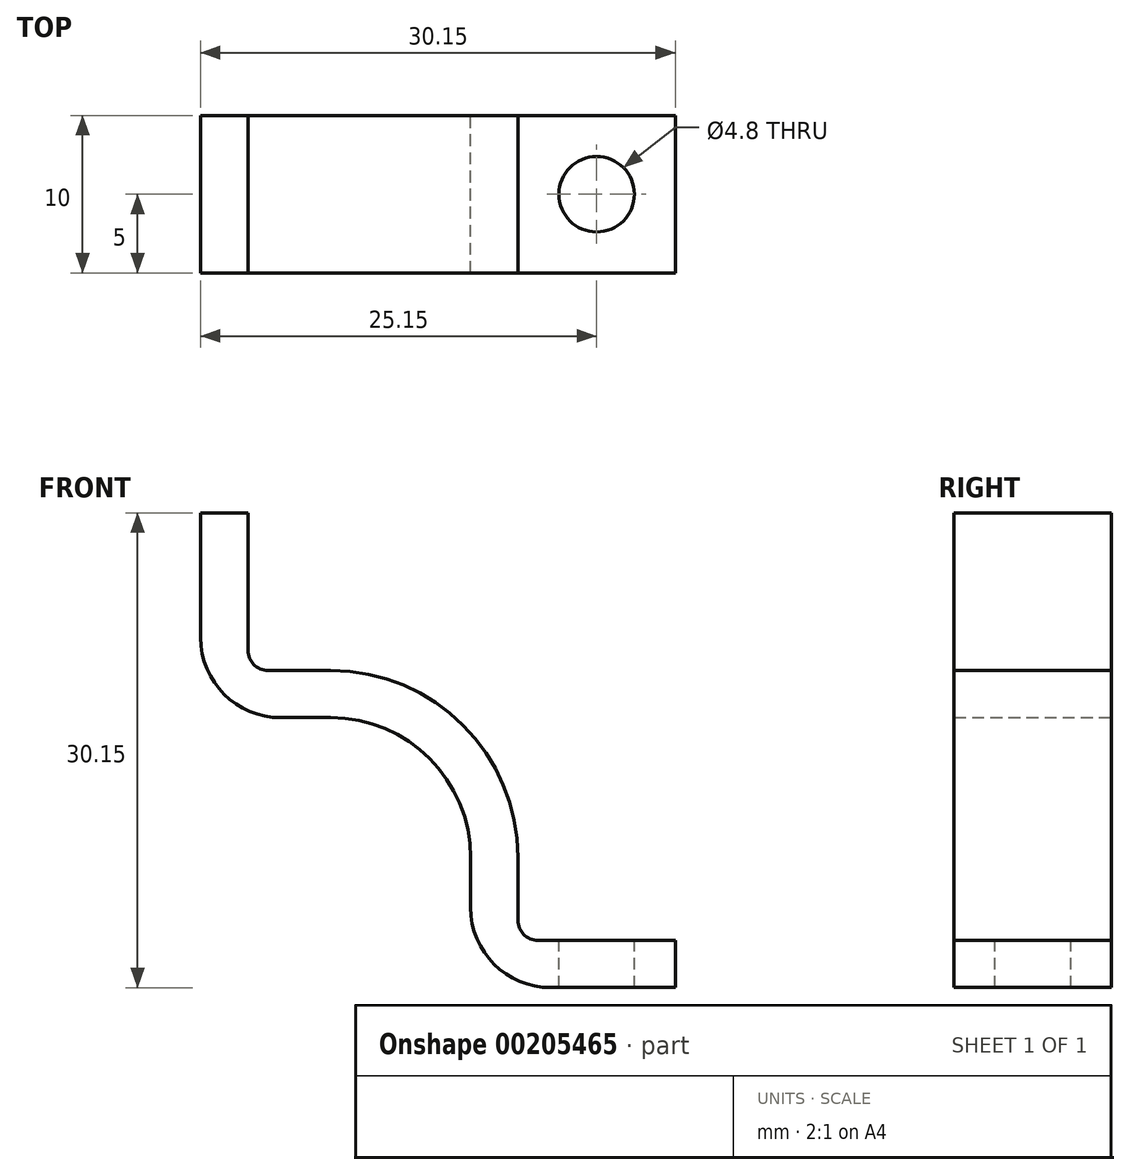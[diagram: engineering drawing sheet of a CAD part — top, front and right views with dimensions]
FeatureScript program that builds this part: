
annotation { "Feature Type Name" : "Feature", "Feature Type Description" : "" }
export const myFeature = defineFeature(function(context is Context, id is Id, definition is map)
    precondition{}
    {
        {
            var Q0;
            Q0=qCreatedBy(makeId("Front.planeOp"),FACE);
            var sketch = newSketch(context, id + "F0", { "sketchPlane" : qUnion([Q0])});
            skArc(sketch, "E0", {"start": v(8.9, 0) * mm, "mid": v(6.29, 6.29) * mm, "end": v(0, 8.9) * mm});
            skLineSegment(sketch, "E1", {"start": v(0, 0) * mm, "end": v(6.29, 6.29) * mm, "construction": true});
            skLineSegment(sketch, "E2", {"start": v(8.89, 0) * mm, "end": v(8.89, -8.26) * mm});
            skLineSegment(sketch, "E3", {"start": v(8.9, -8.26) * mm, "end": v(21.9, -8.25) * mm});
            skLineSegment(sketch, "E4", {"start": v(21.9, -8.25) * mm, "end": v(21.9, -5.25) * mm});
            skLineSegment(sketch, "E5", {"start": v(21.9, -5.25) * mm, "end": v(11.9, -5.25) * mm});
            skLineSegment(sketch, "E6", {"start": v(11.89, -5.25) * mm, "end": v(11.89, 0) * mm});
            skArc(sketch, "E7", {"start": v(11.89, 0) * mm, "mid": v(8.4, 8.4) * mm, "end": v(0, 11.89) * mm});
            skLineSegment(sketch, "E8.MirrorCS", {"start": v(-8.26, 21.9) * mm, "end": v(-5.26, 21.9) * mm});
            skLineSegment(sketch, "E9.MirrorCS", {"start": v(-8.25, 8.89) * mm, "end": v(-8.26, 21.89) * mm});
            skLineSegment(sketch, "E10.MirrorCS", {"start": v(-5.26, 21.89) * mm, "end": v(-5.25, 11.89) * mm});
            skLineSegment(sketch, "E11.MirrorCS", {"start": v(0, 8.89) * mm, "end": v(-8.26, 8.89) * mm});
            skLineSegment(sketch, "E12.MirrorCS", {"start": v(-5.26, 11.89) * mm, "end": v(0, 11.89) * mm});
            skSolve(sketch);
        }
        {
            var Q0;
            Q0=makeQuery(id+"F0.imprint","IMPRINT",FACE,{"disambiguationData":[TD([[makeQuery(id+"F0.imprint","IMPRINT",EDGE,{"derivedFrom":sQuery(id+"F0.wireOp",EDGE,"E0")}),-1.0]])]});
            extrude(context, id + "F1", {"entities" : qUnion([Q0]), "depth" : 10 * mm});
        }
        {
            var Q0;
            Q0=makeQuery(id+"F1.opExtrude","SWEPT_FACE",FACE,{"disambiguationData":[OSD([sQuery(id+"F0.wireOp",EDGE,"E5")])]});
            var sketch = newSketch(context, id + "F2", { "sketchPlane" : qUnion([Q0])});
            skCircle(sketch, "E13", {"center": v(16.9, -5) * mm, "radius": 2.4 * mm});
            skSolve(sketch);
        }
        {
            var Q0;
            Q0 = qSketchRegion(id + "F2", true);
            extrude(context, id + "F3", {"entities" : qUnion([Q0]), "operationType" : NewBodyOperationType.REMOVE, "endBound" : BoundingType.UP_TO_NEXT, "oppositeDirection" : true, "depth" : 25.4 * mm});
        }
        {
            var Q0;
            Q0=makeQuery(id+"F1.opExtrude","CAP_EDGE",EDGE,{"disambiguationData":[OSD([sQuery(id+"F0.wireOp",EDGE,"E0")])],"isStart":true});
            cPoint(context, id + "F4", {"entities" : qUnion([Q0]), "parameter" : 0.5});
        }
        {
            var Q0;
            Q0=makeQuery(id+"F1.opExtrude","CAP_EDGE",EDGE,{"disambiguationData":[OSD([sQuery(id+"F0.wireOp",EDGE,"E0")])],"isStart":false});
            cPoint(context, id + "F5", {"entities" : qUnion([Q0]), "parameter" : 0.5});
        }
        {
            var Q0;
            Q0=qCreatedBy(makeId("Origin.pointOp"),VERTEX);
            var Q1;
            Q1 = qCreatedBy(id + "F4" ,VERTEX);
            var Q2;
            Q2 = qCreatedBy(id + "F5" ,VERTEX);
            cPlane(context, id + "F6", {"entities" : qUnion([Q0, Q1, Q2]), "cplaneType" : CPlaneType.THREE_POINT, "offset" : 25.4 * mm, "width" : 152.4 * mm, "height" : 152.4 * mm});
        }
        {
            var Q0;
            Q0=makeQuery(id+"F1.opExtrude","SWEPT_EDGE",EDGE,{"disambiguationData":[OSD([sQuery(id+"F0.wireOp",EDGE,"E9.MirrorCS"),sQuery(id+"F0.wireOp",EDGE,"E11.MirrorCS")])]});
            var Q1;
            Q1=makeQuery(id+"F1.opExtrude","SWEPT_EDGE",EDGE,{"disambiguationData":[OSD([sQuery(id+"F0.wireOp",EDGE,"E2"),sQuery(id+"F0.wireOp",EDGE,"E3")])]});
            fillet(context, id + "F7", {"entities" : qUnion([Q0, Q1]), "radius" : 5.08 * mm, "tangentPropagation" : true, "allowEdgeOverflow" : false});
        }
        {
            var Q0;
            Q0=makeQuery(id+"F1.opExtrude","SWEPT_EDGE",EDGE,{"disambiguationData":[OSD([sQuery(id+"F0.wireOp",EDGE,"E10.MirrorCS"),sQuery(id+"F0.wireOp",EDGE,"E12.MirrorCS")])]});
            var Q1;
            Q1=makeQuery(id+"F1.opExtrude","SWEPT_EDGE",EDGE,{"disambiguationData":[OSD([sQuery(id+"F0.wireOp",EDGE,"E5"),sQuery(id+"F0.wireOp",EDGE,"E6")])]});
            fillet(context, id + "F8", {"entities" : qUnion([Q0, Q1]), "radius" : 1.27 * mm, "tangentPropagation" : true, "allowEdgeOverflow" : false});
        }
    });
